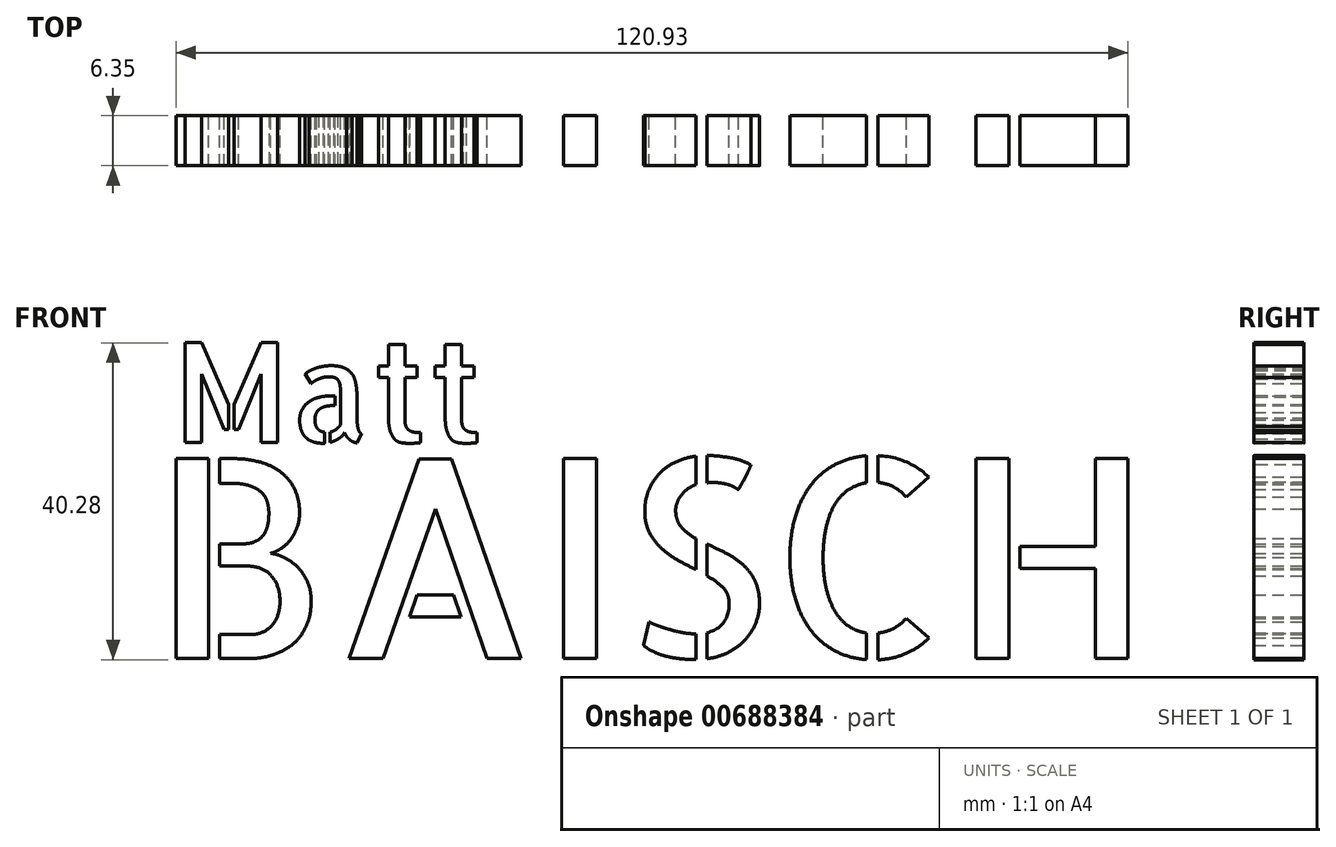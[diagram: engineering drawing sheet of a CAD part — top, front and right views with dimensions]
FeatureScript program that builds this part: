
annotation { "Feature Type Name" : "Feature", "Feature Type Description" : "" }
export const myFeature = defineFeature(function(context is Context, id is Id, definition is map)
    precondition{}
    {
        {
            var Q0;
            Q0=qCreatedBy(makeId("Front.planeOp"),FACE);
            var sketch = newSketch(context, id + "F0", { "sketchPlane" : qUnion([Q0])});
            skText(sketch, "E0", { "text": "BAISCH", "fontName": "AllertaStencil-Regular.ttf"});
            const initialGuessF0  = {"E0": [-0.05204, -0.01392, 1, 0, 0.0254]};
            skSetInitialGuess(sketch, initialGuessF0);
            skSolve(sketch);
        }
        {
            var Q0;
            Q0 = qSketchRegion(id + "F0", true);
            extrude(context, id + "F1", {"entities" : qUnion([Q0]), "depth" : 6.35 * mm, "offsetDistance" : 25.4 * mm});
        }
        {
            var Q0;
            Q0=qCreatedBy(makeId("Front.planeOp"),FACE);
            var sketch = newSketch(context, id + "F2", { "sketchPlane" : qUnion([Q0])});
            skText(sketch, "E1", { "text": "Matt", "fontName": "AllertaStencil-Regular.ttf"});
            const initialGuessF2  = {"E1": [-0.04916, 0.0135, 1, 0, 0.0127]};
            skSetInitialGuess(sketch, initialGuessF2);
            skSolve(sketch);
        }
        {
            var Q0;
            Q0 = qSketchRegion(id + "F2", true);
            extrude(context, id + "F3", {"entities" : qUnion([Q0]), "depth" : 6.35 * mm, "offsetDistance" : 25.4 * mm});
        }
    });
